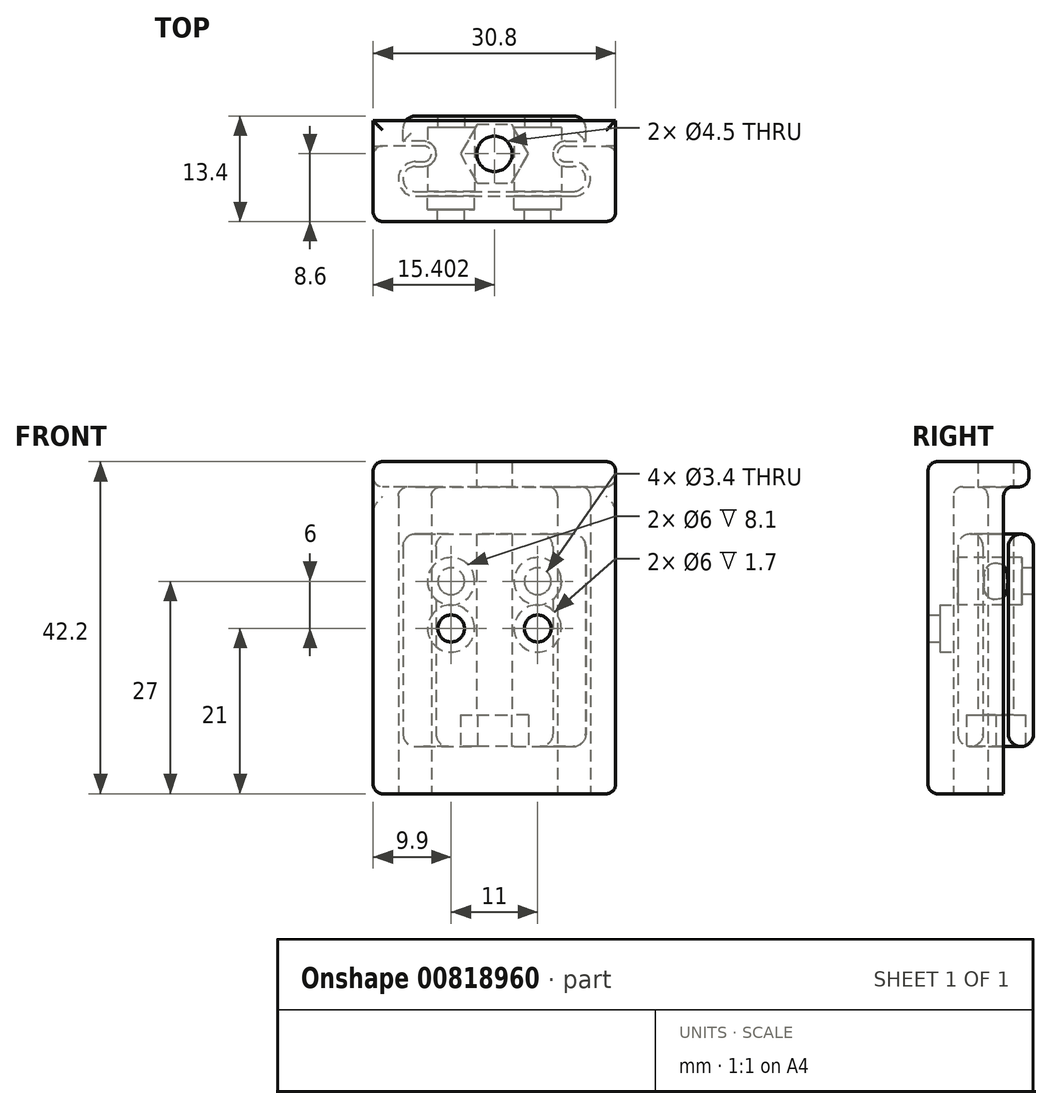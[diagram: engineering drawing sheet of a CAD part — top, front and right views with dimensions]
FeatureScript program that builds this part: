
annotation { "Feature Type Name" : "Feature", "Feature Type Description" : "" }
export const myFeature = defineFeature(function(context is Context, id is Id, definition is map)
    precondition{}
    {
        {
            assignVariable(context, id + "F0", {"name" : "HoleWallD", "anyValue" : 1.5});
        }
        {
            assignVariable(context, id + "F1", {"name" : "RailD", "anyValue" : 3.2});
        }
        {
            assignVariable(context, id + "F2", {"name" : "SliderH", "anyValue" : 21 + 6});
        }
        {
            assignVariable(context, id + "F3", {"name" : "SliderBoltHole", "anyValue" : 4.5});
        }
        {
            assignVariable(context, id + "F4", {"name" : "MountH", "anyValue" : 21 + 6 + 12});
        }
        {
            var Q0;
            Q0=qCreatedBy(makeId("Top.planeOp"),FACE);
            var sketch = newSketch(context, id + "F5", { "sketchPlane" : qUnion([Q0])});
            skArc(sketch, "E0", {"start": v(-9, -0.47) * mm, "mid": v(-7.4, 1.13) * mm, "end": v(-9, 2.73) * mm});
            skLineSegment(sketch, "E1", {"start": v(-9, 2.73) * mm, "end": v(-11.6, 2.73) * mm});
            skLineSegment(sketch, "E2", {"start": v(-11.6, 2.73) * mm, "end": v(-11.6, 5.93) * mm});
            skLineSegment(sketch, "E3", {"start": v(-10, -3.67) * mm, "end": v(0, -3.67) * mm});
            skLineSegment(sketch, "E4", {"start": v(0, 5.93) * mm, "end": v(-11.6, 5.93) * mm});
            skLineSegment(sketch, "E5", {"start": v(-15.4, -7.47) * mm, "end": v(0, -7.47) * mm});
            skLineSegment(sketch, "E6", {"start": v(-10, -0.47) * mm, "end": v(-9, -0.47) * mm});
            skPoint(sketch, "E7", {"position": v(-5.5, 5.93) * mm});
            skPoint(sketch, "E8", {"position": v(-5.5, -7.47) * mm});
            skArc(sketch, "E9", {"start": v(-10, -0.47) * mm, "mid": v(-11.6, -2.07) * mm, "end": v(-10, -3.67) * mm});
            skLineSegment(sketch, "E10.0", {"start": v(-10, -4.27) * mm, "end": v(0, -4.27) * mm});
            skLineSegment(sketch, "E10.1", {"start": v(-9, 2.13) * mm, "end": v(-15.4, 2.13) * mm});
            skArc(sketch, "E10.2", {"start": v(-9, 0.13) * mm, "mid": v(-8, 1.13) * mm, "end": v(-9, 2.13) * mm});
            skLineSegment(sketch, "E10.3", {"start": v(-10, 0.13) * mm, "end": v(-9, 0.13) * mm});
            skArc(sketch, "E10.4", {"start": v(-10, 0.13) * mm, "mid": v(-12.2, -2.07) * mm, "end": v(-10, -4.27) * mm});
            skLineSegment(sketch, "E11", {"start": v(-15.4, 2.13) * mm, "end": v(-15.4, -7.47) * mm});
            skLineSegment(sketch, "E12", {"start": v(0, 5.93) * mm, "end": v(0, 5.93) * mm});
            skLineSegment(sketch, "E13", {"start": v(0, -4.27) * mm, "end": v(0, -7.47) * mm});
            skLineSegment(sketch, "E14.MirrorCS", {"start": v(10, -4.27) * mm, "end": v(0, -4.27) * mm});
            skLineSegment(sketch, "E15.MirrorCS", {"start": v(10, -3.67) * mm, "end": v(0, -3.67) * mm});
            skArc(sketch, "E16.MirrorCS", {"start": v(9, -0.47) * mm, "mid": v(7.4, 1.13) * mm, "end": v(9, 2.73) * mm});
            skLineSegment(sketch, "E17.MirrorCS", {"start": v(9, 2.13) * mm, "end": v(15.4, 2.13) * mm});
            skPoint(sketch, "E18.MirrorP", {"position": v(5.5, 5.93) * mm});
            skLineSegment(sketch, "E19.MirrorCS", {"start": v(15.4, -7.47) * mm, "end": v(0, -7.47) * mm});
            skArc(sketch, "E20.MirrorCS", {"start": v(9, 0.13) * mm, "mid": v(8, 1.13) * mm, "end": v(9, 2.13) * mm});
            skLineSegment(sketch, "E21.MirrorCS", {"start": v(9, 2.73) * mm, "end": v(11.6, 2.73) * mm});
            skLineSegment(sketch, "E22.MirrorCS", {"start": v(9, 0.13) * mm, "end": v(10, 0.13) * mm});
            skLineSegment(sketch, "E23.MirrorCS", {"start": v(0, 5.93) * mm, "end": v(11.6, 5.93) * mm});
            skArc(sketch, "E24.MirrorCS", {"start": v(10, 0.13) * mm, "mid": v(12.2, -2.07) * mm, "end": v(10, -4.27) * mm});
            skLineSegment(sketch, "E25.MirrorCS", {"start": v(11.6, 2.73) * mm, "end": v(11.6, 5.93) * mm});
            skArc(sketch, "E26.MirrorCS", {"start": v(10, -0.47) * mm, "mid": v(11.6, -2.07) * mm, "end": v(10, -3.67) * mm});
            skLineSegment(sketch, "E27.MirrorCS", {"start": v(9, -0.47) * mm, "end": v(10, -0.47) * mm});
            skLineSegment(sketch, "E28.MirrorCS", {"start": v(15.4, 2.13) * mm, "end": v(15.4, -7.47) * mm});
            skPoint(sketch, "E29.MirrorP", {"position": v(5.5, -7.47) * mm});
            skSolve(sketch);
        }
        {
            var Q0;
            Q0=makeQuery(id+"F5.imprint","IMPRINT",FACE,{"disambiguationData":[TD([[makeQuery(id+"F5.imprint","IMPRINT",EDGE,{"derivedFrom":sQuery(id+"F5.wireOp",EDGE,"E0")}),-1.0]])]});
            var Q1;
            {var subQ1=sQuery(id+"F5.wireOp",EDGE,"E15.MirrorCS");Q1=makeQuery(id+"F5.imprint","IMPRINT",FACE,{"disambiguationData":[TD([[makeQuery(id+"F5.imprint","IMPRINT",EDGE,{"derivedFrom":subQ1}),-1.0]])]});}
            extrude(context, id + "F6", {"entities" : qUnion([Q0, Q1]), "endBound" : BoundingType.SYMMETRIC, "depth" : (getVariable(context, 'SliderH')) * mm, "offsetDistance" : 25 * mm});
        }
        {
            var Q0;
            Q0=makeQuery(id+"F6.opExtrude","SWEPT_EDGE",EDGE,{"disambiguationData":[OSD([sQuery(id+"F5.wireOp",EDGE,"E2"),sQuery(id+"F5.wireOp",EDGE,"E4")])]});
            var Q1;
            Q1=makeQuery(id+"F6.opExtrude","SWEPT_EDGE",EDGE,{"disambiguationData":[OSD([sQuery(id+"F5.wireOp",EDGE,"E23.MirrorCS"),sQuery(id+"F5.wireOp",EDGE,"E25.MirrorCS")])]});
            var Q2;
            Q2=makeQuery(id+"F6.opExtrude","CAP_FACE",FACE,{"disambiguationData":[OSD([sQuery(id+"F5.wireOp",EDGE,"E0"),sQuery(id+"F5.wireOp",EDGE,"E1"),sQuery(id+"F5.wireOp",EDGE,"E2"),sQuery(id+"F5.wireOp",EDGE,"E3"),sQuery(id+"F5.wireOp",EDGE,"E4"),sQuery(id+"F5.wireOp",EDGE,"E6"),sQuery(id+"F5.wireOp",EDGE,"E9"),sQuery(id+"F5.wireOp",EDGE,"E15.MirrorCS"),sQuery(id+"F5.wireOp",EDGE,"E16.MirrorCS"),sQuery(id+"F5.wireOp",EDGE,"E21.MirrorCS"),sQuery(id+"F5.wireOp",EDGE,"E23.MirrorCS"),sQuery(id+"F5.wireOp",EDGE,"E25.MirrorCS"),sQuery(id+"F5.wireOp",EDGE,"E26.MirrorCS"),sQuery(id+"F5.wireOp",EDGE,"E27.MirrorCS")])],"isStart":true});
            var Q3;
            Q3=makeQuery(id+"F6.opExtrude","CAP_FACE",FACE,{"disambiguationData":[OSD([sQuery(id+"F5.wireOp",EDGE,"E0"),sQuery(id+"F5.wireOp",EDGE,"E1"),sQuery(id+"F5.wireOp",EDGE,"E2"),sQuery(id+"F5.wireOp",EDGE,"E3"),sQuery(id+"F5.wireOp",EDGE,"E4"),sQuery(id+"F5.wireOp",EDGE,"E6"),sQuery(id+"F5.wireOp",EDGE,"E9"),sQuery(id+"F5.wireOp",EDGE,"E15.MirrorCS"),sQuery(id+"F5.wireOp",EDGE,"E16.MirrorCS"),sQuery(id+"F5.wireOp",EDGE,"E21.MirrorCS"),sQuery(id+"F5.wireOp",EDGE,"E23.MirrorCS"),sQuery(id+"F5.wireOp",EDGE,"E25.MirrorCS"),sQuery(id+"F5.wireOp",EDGE,"E26.MirrorCS"),sQuery(id+"F5.wireOp",EDGE,"E27.MirrorCS")])],"isStart":false});
            fillet(context, id + "F7", {"entities" : qUnion([Q0, Q1, Q2, Q3]), "radius" : 1.6 * mm, "tangentPropagation" : true, "allowEdgeOverflow" : false});
        }
        {
            var Q0;
            Q0=makeQuery(id+"F6.opExtrude","SWEPT_FACE",FACE,{"disambiguationData":[OSD([sQuery(id+"F5.wireOp",EDGE,"E3"),sQuery(id+"F5.wireOp",EDGE,"E15.MirrorCS")])]});
            var sketch = newSketch(context, id + "F8", { "sketchPlane" : qUnion([Q0])});
            skLineSegment(sketch, "E30.bottom", {"start": v(5.5, 7.5) * mm, "end": v(-5.5, 7.5) * mm});
            skLineSegment(sketch, "E30.top", {"start": v(5.5, -7.5) * mm, "end": v(-5.5, -7.5) * mm});
            skLineSegment(sketch, "E30.left", {"start": v(5.5, 7.5) * mm, "end": v(5.5, -7.5) * mm});
            skLineSegment(sketch, "E30.right", {"start": v(-5.5, 7.5) * mm, "end": v(-5.5, -7.5) * mm});
            skPoint(sketch, "E30.middle", {"position": v(0, 0) * mm});
            skSolve(sketch);
        }
        {
            var Q0;
            Q0=makeQuery(id+"F6.opExtrude","CAP_FACE",FACE,{"disambiguationData":[OSD([sQuery(id+"F5.wireOp",EDGE,"E0"),sQuery(id+"F5.wireOp",EDGE,"E1"),sQuery(id+"F5.wireOp",EDGE,"E2"),sQuery(id+"F5.wireOp",EDGE,"E3"),sQuery(id+"F5.wireOp",EDGE,"E4"),sQuery(id+"F5.wireOp",EDGE,"E6"),sQuery(id+"F5.wireOp",EDGE,"E9"),sQuery(id+"F5.wireOp",EDGE,"E12"),sQuery(id+"F5.wireOp",EDGE,"E15.MirrorCS"),sQuery(id+"F5.wireOp",EDGE,"E16.MirrorCS"),sQuery(id+"F5.wireOp",EDGE,"E12"),sQuery(id+"F5.wireOp",EDGE,"E21.MirrorCS"),sQuery(id+"F5.wireOp",EDGE,"E23.MirrorCS"),sQuery(id+"F5.wireOp",EDGE,"E25.MirrorCS"),sQuery(id+"F5.wireOp",EDGE,"E26.MirrorCS"),sQuery(id+"F5.wireOp",EDGE,"E27.MirrorCS")])],"isStart":true});
            var sketch = newSketch(context, id + "F9", { "sketchPlane" : qUnion([Q0])});
            skPoint(sketch, "E31", {"position": v(0, 0) * mm});
            skCircle(sketch, "E32.cCircle", {"center": v(0, -1.13) * mm, "radius": 3.75 * mm, "construction": true});
            skLineSegment(sketch, "E32.0", {"start": v(4.33, -1.13) * mm, "end": v(2.17, -4.88) * mm});
            skLineSegment(sketch, "E32.1", {"start": v(2.17, -4.88) * mm, "end": v(-2.16, -4.88) * mm});
            skLineSegment(sketch, "E32.2", {"start": v(-2.16, -4.88) * mm, "end": v(-4.33, -1.13) * mm});
            skLineSegment(sketch, "E32.3", {"start": v(-4.33, -1.13) * mm, "end": v(-2.16, 2.62) * mm});
            skLineSegment(sketch, "E32.4", {"start": v(-2.16, 2.62) * mm, "end": v(2.17, 2.62) * mm});
            skLineSegment(sketch, "E32.5", {"start": v(2.17, 2.62) * mm, "end": v(4.33, -1.13) * mm});
            skPoint(sketch, "E32.0.midPoint", {"position": v(3.25, -3) * mm});
            skSolve(sketch);
        }
        {
            var Q0;
            Q0=sQuery(id+"F8.wireOp",VERTEX,"E30.right.start");
            var Q1;
            Q1=sQuery(id+"F8.wireOp",VERTEX,"E30.left.start");
            var Q2;
            Q2=makeQuery(id+"F6.opExtrude","SWEPT_BODY",BODY,{"disambiguationData":[OSD([sQuery(id+"F5.wireOp",EDGE,"E0"),sQuery(id+"F5.wireOp",EDGE,"E1"),sQuery(id+"F5.wireOp",EDGE,"E2"),sQuery(id+"F5.wireOp",EDGE,"E3"),sQuery(id+"F5.wireOp",EDGE,"E4"),sQuery(id+"F5.wireOp",EDGE,"E6"),sQuery(id+"F5.wireOp",EDGE,"E9"),sQuery(id+"F5.wireOp",EDGE,"E12"),sQuery(id+"F5.wireOp",EDGE,"E15.MirrorCS"),sQuery(id+"F5.wireOp",EDGE,"E16.MirrorCS"),sQuery(id+"F5.wireOp",EDGE,"E12"),sQuery(id+"F5.wireOp",EDGE,"E21.MirrorCS"),sQuery(id+"F5.wireOp",EDGE,"E23.MirrorCS"),sQuery(id+"F5.wireOp",EDGE,"E25.MirrorCS"),sQuery(id+"F5.wireOp",EDGE,"E26.MirrorCS"),sQuery(id+"F5.wireOp",EDGE,"E27.MirrorCS")])]});
            hole(context, id + "F10", {"style" : HoleStyle.C_BORE, "endStyle" : HoleEndStyle.THROUGH, "holeDiameter" : 3.4 * mm, "cBoreDiameter" : 6 * mm, "cBoreDepth" : ((getVariable(context, 'RailD') * 3) - getVariable(context, 'HoleWallD')) * mm, "majorDiameter" : 5 * mm, "isTappedThrough" : true, "tappedDepth" : 12 * mm, "tapClearance" : 3, "locations" : qUnion([Q0, Q1]), "scope" : qUnion([Q2])});
        }
        {
            var Q0;
            {var subQ4=sQuery(id+"F9.wireOp",EDGE,"E32.2");Q0=makeQuery(id+"F9.imprint","IMPRINT",FACE,{"disambiguationData":[TD([[makeQuery(id+"F9.imprint","IMPRINT",EDGE,{"derivedFrom":subQ4}),-1.0]])]});}
            var Q1;
            {var subQ5=sQuery(id+"F9.wireOp",EDGE,"E32.0");Q1=makeQuery(id+"F9.imprint","IMPRINT",FACE,{"disambiguationData":[TD([[makeQuery(id+"F9.imprint","IMPRINT",EDGE,{"derivedFrom":subQ5}),-1.0]])]});}
            var Q2;
            {var subQ0=sQuery(id+"F9.wireOp",EDGE,"E32.4");Q2=makeQuery(id+"F9.imprint","IMPRINT",FACE,{"disambiguationData":[TD([[makeQuery(id+"F9.imprint","IMPRINT",EDGE,{"derivedFrom":subQ0}),-1.0]])]});}
            var Q3;
            {var subQ0=sQuery(id+"F9.wireOp",EDGE,"E32.5");var subQ1=sQuery(id+"F9.wireOp",EDGE,"E32.0");var subQ2=makeQuery(id+"F9.imprint","INTERSECT",VERTEX,{"derivedFrom":[subQ1,subQ0]});Q3=makeQuery(id+"F9.imprint","IMPRINT",FACE,{"disambiguationData":[TD([[makeQuery(id+"F9.imprint","IMPRINT",EDGE,{"disambiguationData":[TD([[subQ2,-1.0]])],"derivedFrom":subQ1}),-1.0]])]});}
            extrude(context, id + "F11", {"entities" : qUnion([Q0, Q1, Q2, Q3]), "operationType" : NewBodyOperationType.REMOVE, "oppositeDirection" : true, "depth" : 4 * mm, "offsetDistance" : 25 * mm});
        }
        {
            var Q0;
            Q0=sQuery(id+"F9.wireOp",VERTEX,"E32.cCircle.center");
            var Q1;
            Q1=makeQuery(id+"F6.opExtrude","SWEPT_BODY",BODY,{"disambiguationData":[OSD([sQuery(id+"F5.wireOp",EDGE,"E0"),sQuery(id+"F5.wireOp",EDGE,"E1"),sQuery(id+"F5.wireOp",EDGE,"E2"),sQuery(id+"F5.wireOp",EDGE,"E3"),sQuery(id+"F5.wireOp",EDGE,"E4"),sQuery(id+"F5.wireOp",EDGE,"E6"),sQuery(id+"F5.wireOp",EDGE,"E9"),sQuery(id+"F5.wireOp",EDGE,"E12"),sQuery(id+"F5.wireOp",EDGE,"E15.MirrorCS"),sQuery(id+"F5.wireOp",EDGE,"E16.MirrorCS"),sQuery(id+"F5.wireOp",EDGE,"E12"),sQuery(id+"F5.wireOp",EDGE,"E21.MirrorCS"),sQuery(id+"F5.wireOp",EDGE,"E23.MirrorCS"),sQuery(id+"F5.wireOp",EDGE,"E25.MirrorCS"),sQuery(id+"F5.wireOp",EDGE,"E26.MirrorCS"),sQuery(id+"F5.wireOp",EDGE,"E27.MirrorCS")])]});
            hole(context, id + "F12", {"style" : HoleStyle.SIMPLE, "endStyle" : HoleEndStyle.THROUGH, "holeDiameter" : (getVariable(context, 'SliderBoltHole')) * mm, "majorDiameter" : 5 * mm, "isTappedThrough" : true, "tappedDepth" : 12 * mm, "tapClearance" : 3, "locations" : qUnion([Q0]), "scope" : qUnion([Q1])});
        }
        {
            var Q0;
            Q0=makeQuery(id+"F5.imprint","IMPRINT",FACE,{"disambiguationData":[TD([[makeQuery(id+"F5.imprint","IMPRINT",EDGE,{"derivedFrom":sQuery(id+"F5.wireOp",EDGE,"E5")}),1.0]])]});
            var Q1;
            Q1=makeQuery(id+"F5.imprint","IMPRINT",FACE,{"disambiguationData":[TD([[makeQuery(id+"F5.imprint","IMPRINT",EDGE,{"derivedFrom":sQuery(id+"F5.wireOp",EDGE,"E14.MirrorCS")}),1.0]])]});
            extrude(context, id + "F13", {"entities" : qUnion([Q0, Q1]), "endBound" : BoundingType.SYMMETRIC, "depth" : (getVariable(context, 'MountH')) * mm, "offsetDistance" : 25 * mm});
        }
        {
            var Q0;
            Q0=makeQuery(id+"F13.opExtrude","SWEPT_FACE",FACE,{"disambiguationData":[OSD([sQuery(id+"F5.wireOp",EDGE,"E10.0"),sQuery(id+"F5.wireOp",EDGE,"E14.MirrorCS")])]});
            var sketch = newSketch(context, id + "F14", { "sketchPlane" : qUnion([Q0])});
            skLineSegment(sketch, "E33.bottom", {"start": v(-5.5, 1.5) * mm, "end": v(5.5, 1.5) * mm});
            skLineSegment(sketch, "E33.top", {"start": v(5.5, -1.5) * mm, "end": v(-5.5, -1.5) * mm});
            skLineSegment(sketch, "E33.left", {"start": v(-5.5, 1.5) * mm, "end": v(-5.5, -1.5) * mm});
            skLineSegment(sketch, "E33.right", {"start": v(5.5, 1.5) * mm, "end": v(5.5, -1.5) * mm});
            skPoint(sketch, "E33.middle", {"position": v(0, 0) * mm});
            skSolve(sketch);
        }
        {
            var Q0;
            Q0=sQuery(id+"F14.wireOp",VERTEX,"E33.bottom.start");
            var Q1;
            Q1=sQuery(id+"F14.wireOp",VERTEX,"E33.right.start");
            var Q2;
            Q2=makeQuery(id+"F13.opExtrude","SWEPT_BODY",BODY,{"disambiguationData":[OSD([sQuery(id+"F5.wireOp",EDGE,"E5"),sQuery(id+"F5.wireOp",EDGE,"E10.0"),sQuery(id+"F5.wireOp",EDGE,"E10.1"),sQuery(id+"F5.wireOp",EDGE,"E10.2"),sQuery(id+"F5.wireOp",EDGE,"E10.3"),sQuery(id+"F5.wireOp",EDGE,"E10.4"),sQuery(id+"F5.wireOp",EDGE,"E11"),sQuery(id+"F5.wireOp",EDGE,"E14.MirrorCS"),sQuery(id+"F5.wireOp",EDGE,"E17.MirrorCS"),sQuery(id+"F5.wireOp",EDGE,"E19.MirrorCS"),sQuery(id+"F5.wireOp",EDGE,"E20.MirrorCS"),sQuery(id+"F5.wireOp",EDGE,"E22.MirrorCS"),sQuery(id+"F5.wireOp",EDGE,"E24.MirrorCS"),sQuery(id+"F5.wireOp",EDGE,"E28.MirrorCS")])]});
            hole(context, id + "F15", {"style" : HoleStyle.C_BORE, "endStyle" : HoleEndStyle.THROUGH, "holeDiameter" : 3.4 * mm, "cBoreDiameter" : 6 * mm, "cBoreDepth" : (getVariable(context, 'RailD') - getVariable(context, 'HoleWallD')) * mm, "majorDiameter" : 5 * mm, "isTappedThrough" : true, "tappedDepth" : 12 * mm, "tapClearance" : 3, "locations" : qUnion([Q0, Q1]), "scope" : qUnion([Q2])});
        }
        {
            var Q0;
            Q0=makeQuery(id+"F13.opExtrude","CAP_FACE",FACE,{"disambiguationData":[OSD([sQuery(id+"F5.wireOp",EDGE,"E5"),sQuery(id+"F5.wireOp",EDGE,"E10.0"),sQuery(id+"F5.wireOp",EDGE,"E10.1"),sQuery(id+"F5.wireOp",EDGE,"E10.2"),sQuery(id+"F5.wireOp",EDGE,"E10.3"),sQuery(id+"F5.wireOp",EDGE,"E10.4"),sQuery(id+"F5.wireOp",EDGE,"E11"),sQuery(id+"F5.wireOp",EDGE,"E14.MirrorCS"),sQuery(id+"F5.wireOp",EDGE,"E17.MirrorCS"),sQuery(id+"F5.wireOp",EDGE,"E19.MirrorCS"),sQuery(id+"F5.wireOp",EDGE,"E20.MirrorCS"),sQuery(id+"F5.wireOp",EDGE,"E22.MirrorCS"),sQuery(id+"F5.wireOp",EDGE,"E24.MirrorCS"),sQuery(id+"F5.wireOp",EDGE,"E28.MirrorCS")])],"isStart":false});
            var sketch = newSketch(context, id + "F16", { "sketchPlane" : qUnion([Q0])});
            skLineSegment(sketch, "E34.bottom", {"start": v(15.4, -7.47) * mm, "end": v(-15.4, -7.47) * mm});
            skLineSegment(sketch, "E34.top", {"start": v(15.4, 5.33) * mm, "end": v(-15.4, 5.33) * mm});
            skLineSegment(sketch, "E34.left", {"start": v(15.4, -7.47) * mm, "end": v(15.4, 5.33) * mm});
            skLineSegment(sketch, "E34.right", {"start": v(-15.4, -7.47) * mm, "end": v(-15.4, 5.33) * mm});
            skSolve(sketch);
        }
        {
            var Q0;
            Q0=qSketchRegion(id+"F16",true);
            extrude(context, id + "F17", {"entities" : qUnion([Q0]), "operationType" : NewBodyOperationType.ADD, "depth" : (getVariable(context, 'RailD')) * mm, "offsetDistance" : 25 * mm});
        }
        {
            var Q0;
            Q0=makeQuery(id+"F17.opExtrude","CAP_FACE",FACE,{"disambiguationData":[OSD([sQuery(id+"F16.wireOp",EDGE,"E34.bottom"),sQuery(id+"F16.wireOp",EDGE,"E34.top"),sQuery(id+"F16.wireOp",EDGE,"E34.left"),sQuery(id+"F16.wireOp",EDGE,"E34.right")])],"isStart":false});
            var Q1;
            Q1=makeQuery(id+"F17.opExtrude","CAP_FACE",FACE,{"disambiguationData":[OSD([sQuery(id+"F16.wireOp",EDGE,"E34.bottom"),sQuery(id+"F16.wireOp",EDGE,"E34.top"),sQuery(id+"F16.wireOp",EDGE,"E34.left"),sQuery(id+"F16.wireOp",EDGE,"E34.right")])],"isStart":true});
            var Q2;
            Q2=makeQuery(id+"F17.boolean.opBoolean","MERGE",EDGE,{"derivedFrom":[makeQuery(id+"F13.opExtrude","SWEPT_EDGE",EDGE,{"disambiguationData":[OSD([sQuery(id+"F5.wireOp",EDGE,"E19.MirrorCS"),sQuery(id+"F5.wireOp",EDGE,"E28.MirrorCS")])]}),makeQuery(id+"F17.opExtrude","SWEPT_EDGE",EDGE,{"disambiguationData":[OSD([sQuery(id+"F16.wireOp",EDGE,"E34.bottom"),sQuery(id+"F16.wireOp",EDGE,"E34.left")])]})]});
            var Q3;
            Q3=makeQuery(id+"F17.boolean.opBoolean","MERGE",EDGE,{"derivedFrom":[makeQuery(id+"F13.opExtrude","SWEPT_EDGE",EDGE,{"disambiguationData":[OSD([sQuery(id+"F5.wireOp",EDGE,"E5"),sQuery(id+"F5.wireOp",EDGE,"E11")])]}),makeQuery(id+"F17.opExtrude","SWEPT_EDGE",EDGE,{"disambiguationData":[OSD([sQuery(id+"F16.wireOp",EDGE,"E34.bottom"),sQuery(id+"F16.wireOp",EDGE,"E34.right")])]})]});
            var Q4;
            Q4=makeQuery(id+"F13.opExtrude","CAP_EDGE",EDGE,{"disambiguationData":[OSD([sQuery(id+"F5.wireOp",EDGE,"E5"),sQuery(id+"F5.wireOp",EDGE,"E19.MirrorCS")])],"isStart":true});
            var Q5;
            Q5=makeQuery(id+"F13.opExtrude","CAP_EDGE",EDGE,{"disambiguationData":[OSD([sQuery(id+"F5.wireOp",EDGE,"E28.MirrorCS")])],"isStart":true});
            var Q6;
            Q6=makeQuery(id+"F13.opExtrude","CAP_EDGE",EDGE,{"disambiguationData":[OSD([sQuery(id+"F5.wireOp",EDGE,"E11")])],"isStart":true});
            fillet(context, id + "F18", {"entities" : qUnion([Q0, Q1, Q2, Q3, Q4, Q5, Q6]), "radius" : 1.2 * mm, "tangentPropagation" : true, "allowEdgeOverflow" : false});
        }
        {
            var Q0;
            Q0=sQuery(id+"F9.wireOp",VERTEX,"E32.cCircle.center");
            var Q1;
            Q1=makeQuery(id+"F13.opExtrude","SWEPT_BODY",BODY,{"disambiguationData":[OSD([sQuery(id+"F5.wireOp",EDGE,"E5"),sQuery(id+"F5.wireOp",EDGE,"E10.0"),sQuery(id+"F5.wireOp",EDGE,"E10.1"),sQuery(id+"F5.wireOp",EDGE,"E10.2"),sQuery(id+"F5.wireOp",EDGE,"E10.3"),sQuery(id+"F5.wireOp",EDGE,"E10.4"),sQuery(id+"F5.wireOp",EDGE,"E11"),sQuery(id+"F5.wireOp",EDGE,"E14.MirrorCS"),sQuery(id+"F5.wireOp",EDGE,"E17.MirrorCS"),sQuery(id+"F5.wireOp",EDGE,"E19.MirrorCS"),sQuery(id+"F5.wireOp",EDGE,"E20.MirrorCS"),sQuery(id+"F5.wireOp",EDGE,"E22.MirrorCS"),sQuery(id+"F5.wireOp",EDGE,"E24.MirrorCS"),sQuery(id+"F5.wireOp",EDGE,"E28.MirrorCS")])]});
            hole(context, id + "F19", {"style" : HoleStyle.SIMPLE, "endStyle" : HoleEndStyle.THROUGH, "holeDiameter" : (getVariable(context, 'SliderBoltHole')) * mm, "majorDiameter" : 5 * mm, "isTappedThrough" : true, "tappedDepth" : 12 * mm, "tapClearance" : 3, "locations" : qUnion([Q0]), "scope" : qUnion([Q1])});
        }
    });
